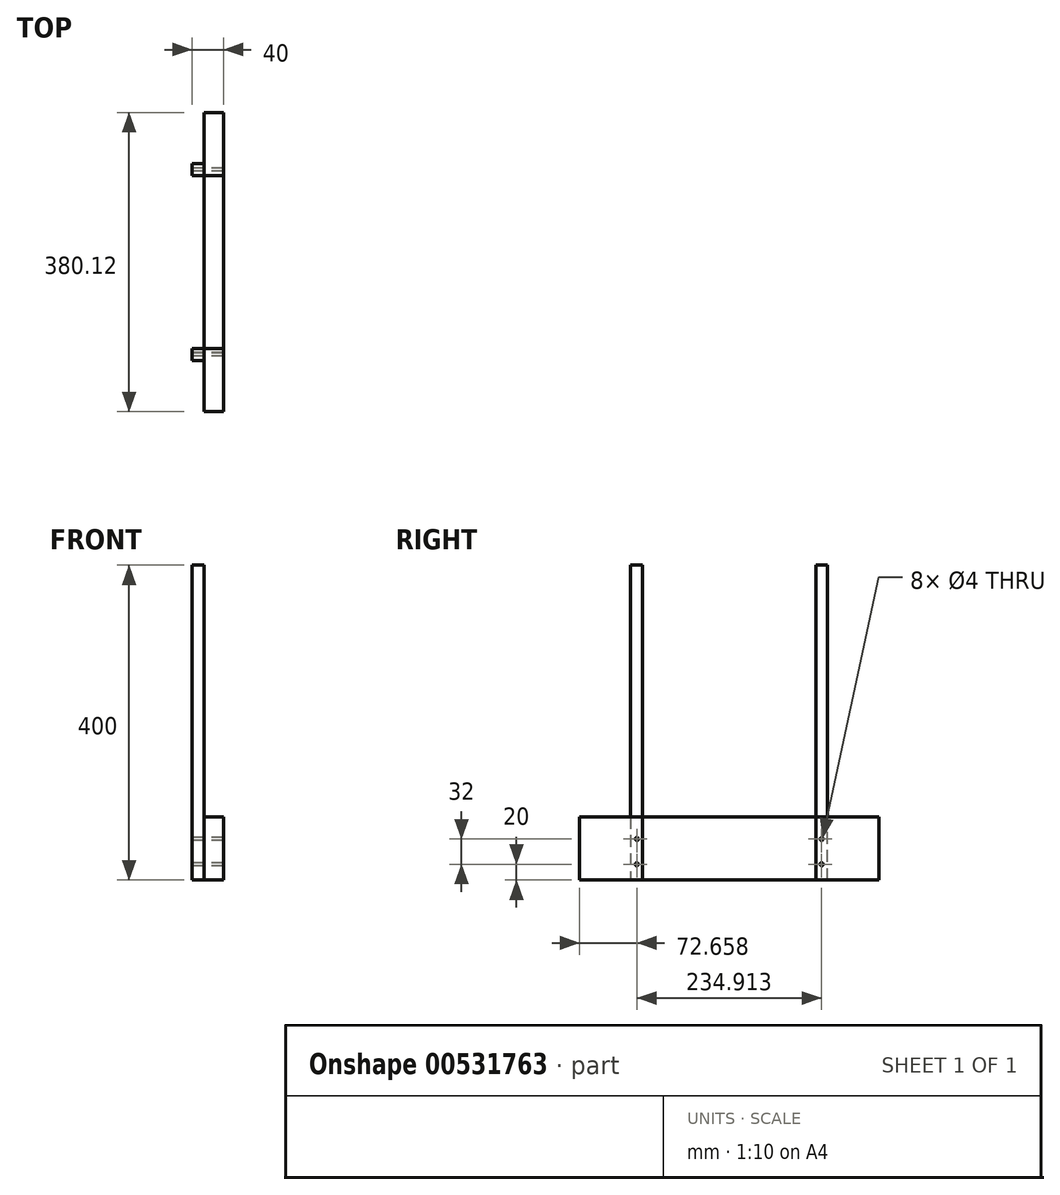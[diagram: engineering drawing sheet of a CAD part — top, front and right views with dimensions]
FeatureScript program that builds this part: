
annotation { "Feature Type Name" : "Feature", "Feature Type Description" : "" }
export const myFeature = defineFeature(function(context is Context, id is Id, definition is map)
    precondition{}
    {
        {
            var Q0;
            Q0=qCreatedBy(makeId("Right.planeOp"),FACE);
            var sketch = newSketch(context, id + "F0", { "sketchPlane" : qUnion([Q0])});
            skLineSegment(sketch, "E0", {"start": v(-167.7, 206.26) * mm, "end": v(-167.7, -193.74) * mm});
            skLineSegment(sketch, "E1", {"start": v(-167.7, -193.74) * mm, "end": v(-152.7, -193.74) * mm});
            skLineSegment(sketch, "E2", {"start": v(-152.7, -193.74) * mm, "end": v(-152.7, 206.26) * mm});
            skLineSegment(sketch, "E3", {"start": v(-152.7, 206.26) * mm, "end": v(-167.7, 206.26) * mm});
            skLineSegment(sketch, "E4", {"start": v(67.3, 206.26) * mm, "end": v(67.3, -193.74) * mm});
            skLineSegment(sketch, "E5", {"start": v(67.3, -193.74) * mm, "end": v(82.3, -193.74) * mm});
            skLineSegment(sketch, "E6", {"start": v(82.3, -193.74) * mm, "end": v(82.3, 206.26) * mm});
            skLineSegment(sketch, "E7", {"start": v(82.3, 206.26) * mm, "end": v(67.3, 206.26) * mm});
            skSolve(sketch);
        }
        {
            var Q0;
            Q0 = qSketchRegion(id + "F0", true);
            extrude(context, id + "F1", {"entities" : qUnion([Q0]), "depth" : 15 * mm, "offsetDistance" : 25 * mm});
        }
        {
            var Q0;
            Q0=makeQuery(id+"F1.opExtrude","CAP_FACE",FACE,{"disambiguationData":[OSD([sQuery(id+"F0.wireOp",EDGE,"E0"),sQuery(id+"F0.wireOp",EDGE,"E1"),sQuery(id+"F0.wireOp",EDGE,"E2"),sQuery(id+"F0.wireOp",EDGE,"E3")])],"isStart":false});
            var sketch = newSketch(context, id + "F2", { "sketchPlane" : qUnion([Q0])});
            skLineSegment(sketch, "E8.bottom", {"start": v(-152.7, -193.74) * mm, "end": v(67.3, -193.74) * mm});
            skLineSegment(sketch, "E8.top", {"start": v(-152.7, -113.57) * mm, "end": v(67.3, -113.57) * mm});
            skLineSegment(sketch, "E8.left", {"start": v(-152.7, -193.74) * mm, "end": v(-152.7, -113.57) * mm});
            skLineSegment(sketch, "E8.right", {"start": v(67.3, -193.74) * mm, "end": v(67.3, -113.57) * mm});
            skSolve(sketch);
        }
        {
            var Q0;
            Q0 = qSketchRegion(id + "F2", true);
            extrude(context, id + "F3", {"entities" : qUnion([Q0]), "depth" : 25 * mm, "offsetDistance" : 25 * mm});
        }
        {
            var Q0;
            Q0=makeQuery(id+"F1.opExtrude","CAP_FACE",FACE,{"disambiguationData":[OSD([sQuery(id+"F0.wireOp",EDGE,"E0"),sQuery(id+"F0.wireOp",EDGE,"E1"),sQuery(id+"F0.wireOp",EDGE,"E2"),sQuery(id+"F0.wireOp",EDGE,"E3")])],"isStart":false});
            var sketch = newSketch(context, id + "F4", { "sketchPlane" : qUnion([Q0])});
            skLineSegment(sketch, "E9.bottom", {"start": v(-152.7, -193.74) * mm, "end": v(-232.7, -193.74) * mm});
            skLineSegment(sketch, "E9.top", {"start": v(-152.7, -113.74) * mm, "end": v(-232.7, -113.74) * mm});
            skLineSegment(sketch, "E9.left", {"start": v(-152.7, -193.74) * mm, "end": v(-152.7, -113.74) * mm});
            skLineSegment(sketch, "E9.right", {"start": v(-232.7, -193.74) * mm, "end": v(-232.7, -113.74) * mm});
            skLineSegment(sketch, "E10.bottom", {"start": v(67.42, -193.74) * mm, "end": v(147.42, -193.74) * mm});
            skLineSegment(sketch, "E10.top", {"start": v(67.42, -113.74) * mm, "end": v(147.42, -113.74) * mm});
            skLineSegment(sketch, "E10.left", {"start": v(67.42, -193.74) * mm, "end": v(67.42, -113.74) * mm});
            skLineSegment(sketch, "E10.right", {"start": v(147.42, -193.74) * mm, "end": v(147.42, -113.74) * mm});
            skSolve(sketch);
        }
        {
            var Q0;
            Q0 = qSketchRegion(id + "F4", true);
            extrude(context, id + "F5", {"entities" : qUnion([Q0]), "depth" : 25 * mm, "offsetDistance" : 25 * mm});
        }
        {
            var Q0;
            Q0=makeQuery(id+"F1.opExtrude","CAP_FACE",FACE,{"disambiguationData":[OSD([sQuery(id+"F0.wireOp",EDGE,"E4"),sQuery(id+"F0.wireOp",EDGE,"E5"),sQuery(id+"F0.wireOp",EDGE,"E6"),sQuery(id+"F0.wireOp",EDGE,"E7")])],"isStart":true});
            var sketch = newSketch(context, id + "F6", { "sketchPlane" : qUnion([Q0])});
            skCircle(sketch, "E11", {"center": v(-74.87, -141.74) * mm, "radius": 2 * mm});
            skCircle(sketch, "E12", {"center": v(159.84, -141.74) * mm, "radius": 2 * mm});
            skCircle(sketch, "E13", {"center": v(-74.8, -173.74) * mm, "radius": 2 * mm});
            skCircle(sketch, "E14", {"center": v(160.04, -173.74) * mm, "radius": 2 * mm});
            skSolve(sketch);
        }
        {
            var Q0;
            Q0 = qSketchRegion(id + "F6", true);
            extrude(context, id + "F7", {"entities" : qUnion([Q0]), "operationType" : NewBodyOperationType.REMOVE, "oppositeDirection" : true, "depth" : 100 * mm, "offsetDistance" : 25 * mm});
        }
    });
